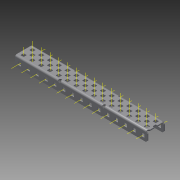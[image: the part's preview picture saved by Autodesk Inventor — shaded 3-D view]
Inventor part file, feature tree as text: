
AUTODESK INVENTOR PART (.ipt)
format: ipt  version: 2015 (Build 190159000, 159)  size: 2,022,912 bytes
history: native  units: in
note: dims shown in document units (in); Inventor stores cm internally (conversion verified against a paired STEP export)
features: other x81, pattern_linear x3, sheet_metal_op x1, extrude x1, imported_body x1, sketch x1
ambient origin geometry x8: Origin, YZ Plane, XZ Plane, XY Plane, X Axis, Y Axis, Z Axis, Center Point
bodies: Body1 (feature_tree)
feature tree (88):
  sheet_metal_op  "Fold1"
  other  "C-Channel"
  extrude  "length cut"  Depth=0.5in
  other  "top axis"
  other  "inner axis"
  other  "front axis"
  other  "back axis"
  pattern_linear  "top axes"  Spacing1=0.5in  [1 undecoded]
  pattern_linear  "inner axes"  Spacing1=0.5in  [1 undecoded]
  pattern_linear  "horiz axes"  Spacing1=-7.5in  [1 undecoded]
  other  "right plane"
  imported_body  "Base1"
  sketch  "Sketch1"  dims[d1=0.0in d4=0.5in d5=0.7874in d7=0.5in d10=0.5in d13=0.5in d14=-7.5in d15=0.0in d16=0.0in d17=0.0in d18=0.0in d19=0.0in]
  other  "Work Point1"
  other  "Work Point2"
  other  "Work Point3"
  other  "Work Point4"
  other  "Work Axis5"
  other  "Work Axis6"
  other  "Work Axis7"
  other  "Work Axis8"
  other  "Work Axis11"
  other  "Work Axis12"
  other  "Work Axis13"
  other  "Work Axis14"
  other  "Work Axis15"
  other  "Work Axis18"
  other  "Work Axis19"
  other  "Work Axis20"
  other  "Work Axis23"
  other  "Work Axis24"
  other  "Work Axis25"
  other  "Work Axis26"
  other  "Work Axis30"
  other  "Work Axis31"
  other  "Work Axis32"
  other  "Work Axis33"
  other  "left plane"
  other  "Work Axis37"
  other  "Work Axis38"
  other  "Work Axis39"
  other  "Work Axis40"
  other  "Work Axis41"
  other  "Work Axis42"
  other  "Work Axis43"
  other  "Work Axis44"
  other  "Work Axis45"
  other  "Work Axis46"
  other  "Work Axis57"
  other  "Work Axis58"
  other  "Work Axis59"
  other  "Work Axis60"
  other  "Work Axis61"
  other  "Work Axis62"
  other  "Work Axis63"
  other  "Work Axis64"
  other  "Work Axis65"
  other  "Work Axis66"
  other  "Work Axis77"
  other  "Work Axis78"
  other  "Work Axis79"
  other  "Work Axis80"
  other  "Work Axis81"
  other  "Work Axis82"
  other  "Work Axis83"
  other  "Work Axis84"
  other  "Work Axis85"
  other  "Work Axis86"
  other  "Work Axis97"
  other  "Work Axis98"
  other  "Work Axis99"
  other  "Work Axis100"
  other  "Work Axis101"
  other  "Work Axis102"
  other  "Work Axis103"
  other  "Work Axis104"
  other  "Work Axis105"
  other  "Work Axis106"
  other  "Work Axis117"
  other  "Work Axis118"
  other  "Work Axis119"
  other  "Work Axis120"
  other  "Work Axis121"
  other  "Work Axis122"
  other  "Work Axis123"
  other  "Work Axis124"
  other  "Work Axis125"
  other  "Work Axis126"
note: 3 required parameter values undecoded (feature->parameter linkage not recoverable at this tier; creation-order binding heuristic only, values carry confidence <= 0.55)
